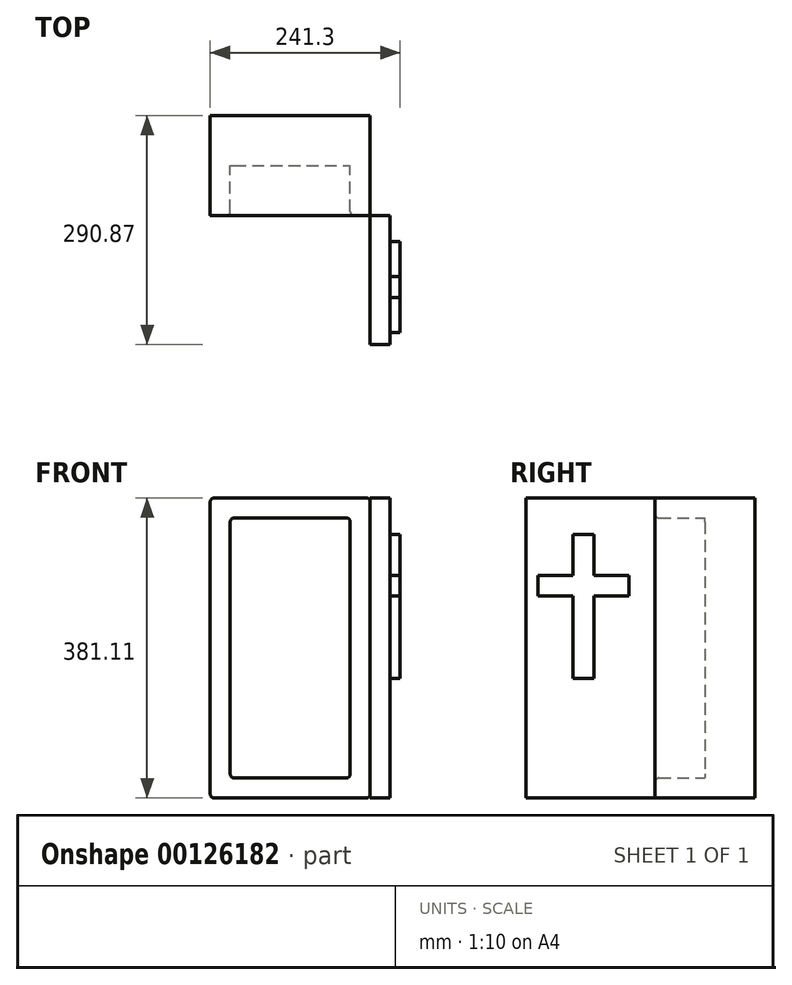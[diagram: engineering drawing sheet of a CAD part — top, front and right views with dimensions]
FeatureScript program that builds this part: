
annotation { "Feature Type Name" : "Feature", "Feature Type Description" : "" }
export const myFeature = defineFeature(function(context is Context, id is Id, definition is map)
    precondition{}
    {
        {
            var Q0;
            Q0=qCreatedBy(makeId("Front.planeOp"),FACE);
            var sketch = newSketch(context, id + "F0", { "sketchPlane" : qUnion([Q0])});
            skLineSegment(sketch, "E0.bottom", {"start": v(-67.62, 116.5) * mm, "end": v(135.58, 116.5) * mm});
            skLineSegment(sketch, "E0.top", {"start": v(-67.62, -264.62) * mm, "end": v(135.58, -264.62) * mm});
            skLineSegment(sketch, "E0.left", {"start": v(-67.62, 116.5) * mm, "end": v(-67.62, -264.62) * mm});
            skLineSegment(sketch, "E0.right", {"start": v(135.58, 116.5) * mm, "end": v(135.58, -264.62) * mm});
            skSolve(sketch);
        }
        {
            var Q0;
            Q0 = qSketchRegion(id + "F0", true);
            extrude(context, id + "F1", {"entities" : qUnion([Q0]), "depth" : 127 * mm});
        }
        {
            var Q0;
            Q0=makeQuery(id+"F1.opExtrude","CAP_FACE",FACE,{"disambiguationData":[OSD([sQuery(id+"F0.wireOp",EDGE,"E0.bottom"),sQuery(id+"F0.wireOp",EDGE,"E0.top"),sQuery(id+"F0.wireOp",EDGE,"E0.left"),sQuery(id+"F0.wireOp",EDGE,"E0.right")])],"isStart":false});
            var Q1;
            Q1=makeQuery(id+"F1.opExtrude","SWEPT_BODY",BODY,{"disambiguationData":[OSD([sQuery(id+"F0.wireOp",EDGE,"E0.bottom"),sQuery(id+"F0.wireOp",EDGE,"E0.top"),sQuery(id+"F0.wireOp",EDGE,"E0.left"),sQuery(id+"F0.wireOp",EDGE,"E0.right")])]});
            shell(context, id + "F2", {"entities" : qUnion([Q0]), "parts" : qUnion([Q1]), "thickness" : 25.4 * mm});
        }
        {
            var Q0;
            Q0=makeQuery(id+"F1.opExtrude","SWEPT_FACE",FACE,{"disambiguationData":[OSD([sQuery(id+"F0.wireOp",EDGE,"E0.right")])]});
            var sketch = newSketch(context, id + "F3", { "sketchPlane" : qUnion([Q0])});
            skLineSegment(sketch, "E1", {"start": v(-127, -264.62) * mm, "end": v(-290.87, -264.62) * mm});
            skLineSegment(sketch, "E2", {"start": v(-290.87, -264.62) * mm, "end": v(-290.87, 116.5) * mm});
            skLineSegment(sketch, "E3", {"start": v(-290.87, 116.5) * mm, "end": v(-127, 116.5) * mm});
            skLineSegment(sketch, "E4", {"start": v(-127, 116.5) * mm, "end": v(-127, -264.62) * mm});
            skSolve(sketch);
        }
        {
            var Q0;
            Q0 = qSketchRegion(id + "F3", true);
            extrude(context, id + "F4", {"entities" : qUnion([Q0]), "operationType" : NewBodyOperationType.ADD, "depth" : 25.4 * mm});
        }
        {
            var Q0;
            Q0=makeQuery(id+"F2.opShell","OFFSET_FACE",FACE,{"disambiguationData":[OSD([sQuery(id+"F0.wireOp",EDGE,"E0.bottom"),sQuery(id+"F0.wireOp",EDGE,"E0.top"),sQuery(id+"F0.wireOp",EDGE,"E0.left"),sQuery(id+"F0.wireOp",EDGE,"E0.right")])]});
            var sketch = newSketch(context, id + "F5", { "sketchPlane" : qUnion([Q0])});
            skLineSegment(sketch, "E5", {"start": v(-42.22, 91.1) * mm, "end": v(110.18, 91.1) * mm});
            skLineSegment(sketch, "E6", {"start": v(110.18, 91.1) * mm, "end": v(110.18, -239.22) * mm});
            skLineSegment(sketch, "E7", {"start": v(110.18, -239.22) * mm, "end": v(-42.22, -239.22) * mm});
            skLineSegment(sketch, "E8", {"start": v(-42.22, 91.1) * mm, "end": v(-42.22, -239.22) * mm});
            skSolve(sketch);
        }
        {
            var Q0;
            Q0 = qSketchRegion(id + "F5", true);
            extrude(context, id + "F6", {"entities" : qUnion([Q0]), "operationType" : NewBodyOperationType.ADD, "depth" : 38.1 * mm});
        }
        {
            var Q0;
            Q0=makeQuery(id+"F1.opExtrude","SWEPT_EDGE",EDGE,{"disambiguationData":[OSD([sQuery(id+"F0.wireOp",EDGE,"E0.top"),sQuery(id+"F0.wireOp",EDGE,"E0.left")])]});
            var Q1;
            Q1=makeQuery(id+"F1.opExtrude","SWEPT_EDGE",EDGE,{"disambiguationData":[OSD([sQuery(id+"F0.wireOp",EDGE,"E0.top"),sQuery(id+"F0.wireOp",EDGE,"E0.right")])]});
            var Q2;
            Q2=makeQuery(id+"F1.opExtrude","SWEPT_EDGE",EDGE,{"disambiguationData":[OSD([sQuery(id+"F0.wireOp",EDGE,"E0.bottom"),sQuery(id+"F0.wireOp",EDGE,"E0.right")])]});
            var Q3;
            Q3=makeQuery(id+"F1.opExtrude","SWEPT_EDGE",EDGE,{"disambiguationData":[OSD([sQuery(id+"F0.wireOp",EDGE,"E0.bottom"),sQuery(id+"F0.wireOp",EDGE,"E0.left")])]});
            var Q4;
            {var subQ0=sQuery(id+"F0.wireOp",EDGE,"E0.bottom");Q4=makeQuery(id+"F2.opShell","OFFSET_EDGE",EDGE,{"disambiguationData":[OSD([subQ0]),TDD([makeQuery(id+"F1.opExtrude","CAP_EDGE",EDGE,{"disambiguationData":[OSD([subQ0])],"isStart":false})])]});}
            var Q5;
            {var subQ0=sQuery(id+"F0.wireOp",EDGE,"E0.right");Q5=makeQuery(id+"F2.opShell","OFFSET_EDGE",EDGE,{"disambiguationData":[OSD([subQ0]),TDD([makeQuery(id+"F1.opExtrude","CAP_EDGE",EDGE,{"disambiguationData":[OSD([subQ0])],"isStart":false})])]});}
            var Q6;
            {var subQ0=sQuery(id+"F0.wireOp",EDGE,"E0.top");Q6=makeQuery(id+"F2.opShell","OFFSET_EDGE",EDGE,{"disambiguationData":[OSD([subQ0]),TDD([makeQuery(id+"F1.opExtrude","CAP_EDGE",EDGE,{"disambiguationData":[OSD([subQ0])],"isStart":false})])]});}
            var Q7;
            {var subQ0=sQuery(id+"F0.wireOp",EDGE,"E0.left");Q7=makeQuery(id+"F2.opShell","OFFSET_EDGE",EDGE,{"disambiguationData":[OSD([subQ0]),TDD([makeQuery(id+"F1.opExtrude","CAP_EDGE",EDGE,{"disambiguationData":[OSD([subQ0])],"isStart":false})])]});}
            var Q8;
            Q8=makeQuery(id+"F6.opExtrude","CAP_EDGE",EDGE,{"disambiguationData":[OSD([sQuery(id+"F5.wireOp",EDGE,"E8")])],"isStart":false});
            var Q9;
            Q9=makeQuery(id+"F6.opExtrude","CAP_EDGE",EDGE,{"disambiguationData":[OSD([sQuery(id+"F5.wireOp",EDGE,"E5")])],"isStart":false});
            var Q10;
            Q10=makeQuery(id+"F2.opShell","OFFSET_EDGE",EDGE,{"disambiguationData":[OSD([sQuery(id+"F0.wireOp",EDGE,"E0.bottom"),sQuery(id+"F0.wireOp",EDGE,"E0.left")])]});
            var Q11;
            Q11=makeQuery(id+"F2.opShell","OFFSET_EDGE",EDGE,{"disambiguationData":[OSD([sQuery(id+"F0.wireOp",EDGE,"E0.bottom"),sQuery(id+"F0.wireOp",EDGE,"E0.right")])]});
            var Q12;
            Q12=makeQuery(id+"F6.opExtrude","CAP_EDGE",EDGE,{"disambiguationData":[OSD([sQuery(id+"F5.wireOp",EDGE,"E6")])],"isStart":false});
            var Q13;
            Q13=makeQuery(id+"F2.opShell","OFFSET_EDGE",EDGE,{"disambiguationData":[OSD([sQuery(id+"F0.wireOp",EDGE,"E0.top"),sQuery(id+"F0.wireOp",EDGE,"E0.right")])]});
            var Q14;
            Q14=makeQuery(id+"F6.opExtrude","CAP_EDGE",EDGE,{"disambiguationData":[OSD([sQuery(id+"F5.wireOp",EDGE,"E7")])],"isStart":false});
            var Q15;
            Q15=makeQuery(id+"F2.opShell","OFFSET_EDGE",EDGE,{"disambiguationData":[OSD([sQuery(id+"F0.wireOp",EDGE,"E0.top"),sQuery(id+"F0.wireOp",EDGE,"E0.left")])]});
            fillet(context, id + "F7", {"entities" : qUnion([Q0, Q1, Q2, Q3, Q4, Q5, Q6, Q7, Q8, Q9, Q10, Q11, Q12, Q13, Q14, Q15]), "radius" : 5.08 * mm, "tangentPropagation" : true, "allowEdgeOverflow" : false});
        }
        {
            var Q0;
            Q0=makeQuery(id+"F4.opExtrude","CAP_FACE",FACE,{"disambiguationData":[OSD([sQuery(id+"F3.wireOp",EDGE,"E1"),sQuery(id+"F3.wireOp",EDGE,"E2"),sQuery(id+"F3.wireOp",EDGE,"E3"),sQuery(id+"F3.wireOp",EDGE,"E4")])],"isStart":false});
            var sketch = newSketch(context, id + "F8", { "sketchPlane" : qUnion([Q0])});
            skLineSegment(sketch, "E9", {"start": v(-231.3, 70.02) * mm, "end": v(-231.3, 18.1) * mm});
            skLineSegment(sketch, "E10", {"start": v(-231.3, 18.1) * mm, "end": v(-275.75, 18.1) * mm});
            skLineSegment(sketch, "E11", {"start": v(-275.75, 18.1) * mm, "end": v(-275.75, -8.08) * mm});
            skLineSegment(sketch, "E12", {"start": v(-275.75, -8.08) * mm, "end": v(-231.3, -8.08) * mm});
            skLineSegment(sketch, "E13", {"start": v(-231.3, -8.08) * mm, "end": v(-231.3, -112.76) * mm});
            skLineSegment(sketch, "E14", {"start": v(-231.3, -112.76) * mm, "end": v(-204.71, -112.76) * mm});
            skLineSegment(sketch, "E15", {"start": v(-204.71, -112.76) * mm, "end": v(-204.71, -8.08) * mm});
            skLineSegment(sketch, "E16", {"start": v(-204.71, -8.08) * mm, "end": v(-160.26, -8.08) * mm});
            skLineSegment(sketch, "E17", {"start": v(-160.26, -8.08) * mm, "end": v(-160.26, 18.1) * mm});
            skLineSegment(sketch, "E18", {"start": v(-160.26, 18.1) * mm, "end": v(-204.71, 18.1) * mm});
            skLineSegment(sketch, "E19", {"start": v(-204.71, 18.1) * mm, "end": v(-204.71, 70.02) * mm});
            skLineSegment(sketch, "E20", {"start": v(-204.71, 70.02) * mm, "end": v(-231.3, 70.02) * mm});
            skSolve(sketch);
        }
        {
            var Q0;
            Q0 = qSketchRegion(id + "F8", true);
            extrude(context, id + "F9", {"entities" : qUnion([Q0]), "depth" : 12.7 * mm});
        }
    });
